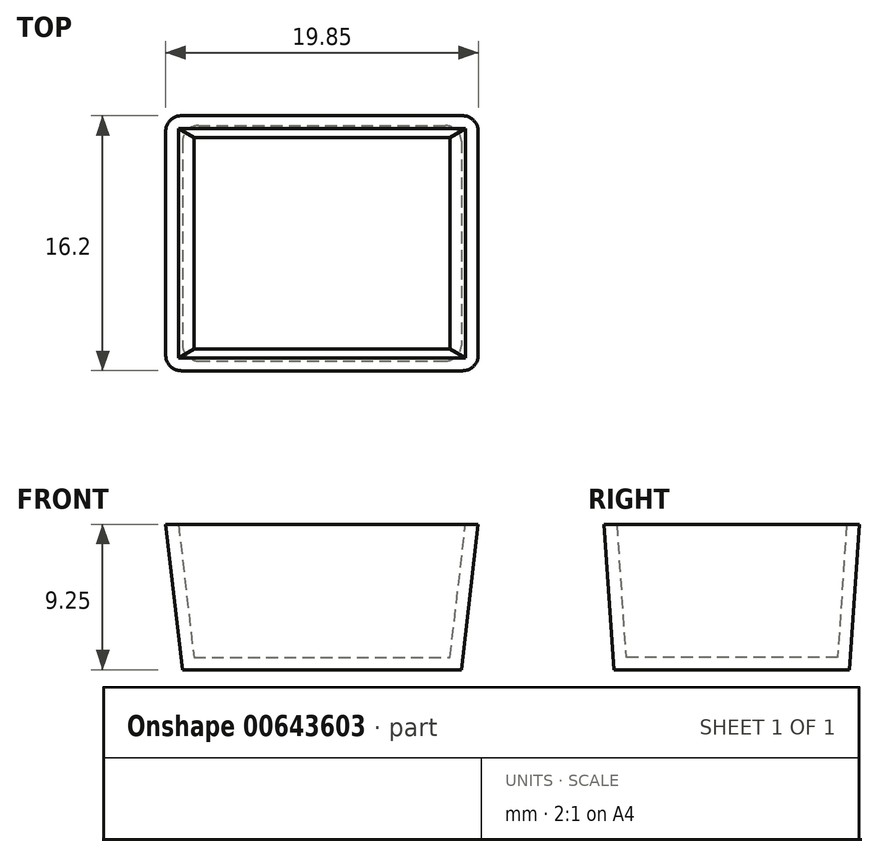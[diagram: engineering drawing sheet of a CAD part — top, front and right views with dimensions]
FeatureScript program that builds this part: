
annotation { "Feature Type Name" : "Feature", "Feature Type Description" : "" }
export const myFeature = defineFeature(function(context is Context, id is Id, definition is map)
    precondition{}
    {
        {
            assignVariable(context, id + "F0", {"name" : "z", "anyValue" : 9.25});
        }
        {
            assignVariable(context, id + "F1", {"name" : "wall", "anyValue" : 0.8});
        }
        {
            var Q0;
            Q0=qCreatedBy(makeId("Top.planeOp"),FACE);
            var sketch = newSketch(context, id + "F2", { "sketchPlane" : qUnion([Q0])});
            skLineSegment(sketch, "E0.bottom", {"start": v(-250.5, 118.24) * mm, "end": v(-232.8, 118.24) * mm});
            skLineSegment(sketch, "E0.top", {"start": v(-250.5, 103.3) * mm, "end": v(-232.8, 103.3) * mm});
            skLineSegment(sketch, "E0.left", {"start": v(-250.5, 118.24) * mm, "end": v(-250.5, 103.3) * mm});
            skLineSegment(sketch, "E0.right", {"start": v(-232.8, 118.24) * mm, "end": v(-232.8, 103.3) * mm});
            skSolve(sketch);
        }
        {
            var Q0;
            Q0=makeQuery(id+"F2.imprint","IMPRINT",FACE,{"disambiguationData":[TD([[makeQuery(id+"F2.imprint","IMPRINT",EDGE,{"derivedFrom":sQuery(id+"F2.wireOp",EDGE,"E0.bottom")}),-1.0]])]});
            cPlane(context, id + "F3", {"entities" : qUnion([Q0]), "cplaneType" : CPlaneType.OFFSET, "offset" : (getVariable(context, 'z')) * mm, "width" : 150 * mm, "height" : 150 * mm});
        }
        {
            var Q0;
            Q0=qCreatedBy(id+"F3.planeOp",FACE);
            var sketch = newSketch(context, id + "F4", { "sketchPlane" : qUnion([Q0])});
            skLineSegment(sketch, "E1.0.0", {"start": v(-250.5, 118.24) * mm, "end": v(-250.5, 103.3) * mm, "construction": true});
            skLineSegment(sketch, "E1.0.1", {"start": v(-250.5, 103.3) * mm, "end": v(-232.8, 103.3) * mm, "construction": true});
            skLineSegment(sketch, "E1.0.2", {"start": v(-232.8, 103.3) * mm, "end": v(-232.8, 118.24) * mm, "construction": true});
            skLineSegment(sketch, "E1.0.3", {"start": v(-232.8, 118.24) * mm, "end": v(-250.5, 118.24) * mm, "construction": true});
            skLineSegment(sketch, "E2", {"start": v(-250.5, 103.3) * mm, "end": v(-232.8, 118.24) * mm, "construction": true});
            skLineSegment(sketch, "E3", {"start": v(-250.5, 118.24) * mm, "end": v(-232.8, 103.3) * mm, "construction": true});
            skPoint(sketch, "E4", {"position": v(-241.66, 110.77) * mm});
            skLineSegment(sketch, "E5.bottom", {"start": v(-231.73, 118.87) * mm, "end": v(-251.58, 118.87) * mm});
            skLineSegment(sketch, "E5.top", {"start": v(-231.73, 102.67) * mm, "end": v(-251.58, 102.67) * mm});
            skLineSegment(sketch, "E5.left", {"start": v(-231.73, 118.87) * mm, "end": v(-231.73, 102.67) * mm});
            skLineSegment(sketch, "E5.right", {"start": v(-251.58, 118.87) * mm, "end": v(-251.58, 102.67) * mm});
            skSolve(sketch);
        }
        {
            var Q0;
            Q0=makeQuery(id+"F2.imprint","IMPRINT",FACE,{"disambiguationData":[TD([[makeQuery(id+"F2.imprint","IMPRINT",EDGE,{"derivedFrom":sQuery(id+"F2.wireOp",EDGE,"E0.bottom")}),-1.0]])]});
            var Q1;
            Q1=makeQuery(id+"F4.imprint","IMPRINT",FACE,{"disambiguationData":[TD([[makeQuery(id+"F4.imprint","IMPRINT",EDGE,{"derivedFrom":sQuery(id+"F4.wireOp",EDGE,"E5.bottom")}),1.0]])]});
            loft(context, id + "F5", {"sheetProfilesArray" : [{ "sheetProfileEntities" : qUnion([Q0]) }, { "sheetProfileEntities" : qUnion([Q1]) }]});
        }
        {
            var Q0;
            Q0=makeQuery(id+"F5.opLoft","CAP_FACE",FACE,{"disambiguationData":[OSD([makeQuery(id+"F4.imprint","IMPRINT",FACE,{"disambiguationData":[TD([[makeQuery(id+"F4.imprint","IMPRINT",EDGE,{"derivedFrom":sQuery(id+"F4.wireOp",EDGE,"E5.bottom")}),1.0]])]})])],"isStart":true});
            shell(context, id + "F6", {"entities" : qUnion([Q0]), "thickness" : (getVariable(context, 'wall')) * mm});
        }
        {
            var Q0;
            Q0=makeQuery(id+"F5.opLoft","SWEPT_EDGE",EDGE,{"disambiguationData":[OSD([sQuery(id+"F2.wireOp",EDGE,"E0.top"),sQuery(id+"F2.wireOp",EDGE,"E0.left"),sQuery(id+"F4.wireOp",EDGE,"E5.top"),sQuery(id+"F4.wireOp",EDGE,"E5.right")])]});
            var Q1;
            Q1=makeQuery(id+"F5.opLoft","SWEPT_EDGE",EDGE,{"disambiguationData":[OSD([sQuery(id+"F2.wireOp",EDGE,"E0.top"),sQuery(id+"F2.wireOp",EDGE,"E0.right"),sQuery(id+"F4.wireOp",EDGE,"E5.top"),sQuery(id+"F4.wireOp",EDGE,"E5.left")])]});
            var Q2;
            Q2=makeQuery(id+"F5.opLoft","SWEPT_EDGE",EDGE,{"disambiguationData":[OSD([sQuery(id+"F2.wireOp",EDGE,"E0.bottom"),sQuery(id+"F2.wireOp",EDGE,"E0.right"),sQuery(id+"F4.wireOp",EDGE,"E5.bottom"),sQuery(id+"F4.wireOp",EDGE,"E5.left")])]});
            var Q3;
            Q3=makeQuery(id+"F5.opLoft","SWEPT_EDGE",EDGE,{"disambiguationData":[OSD([sQuery(id+"F2.wireOp",EDGE,"E0.bottom"),sQuery(id+"F2.wireOp",EDGE,"E0.left"),sQuery(id+"F4.wireOp",EDGE,"E5.bottom"),sQuery(id+"F4.wireOp",EDGE,"E5.right")])]});
            fillet(context, id + "F7", {"entities" : qUnion([Q0, Q1, Q2, Q3]), "radius" : 1 * mm, "tangentPropagation" : true, "allowEdgeOverflow" : false});
        }
    });
